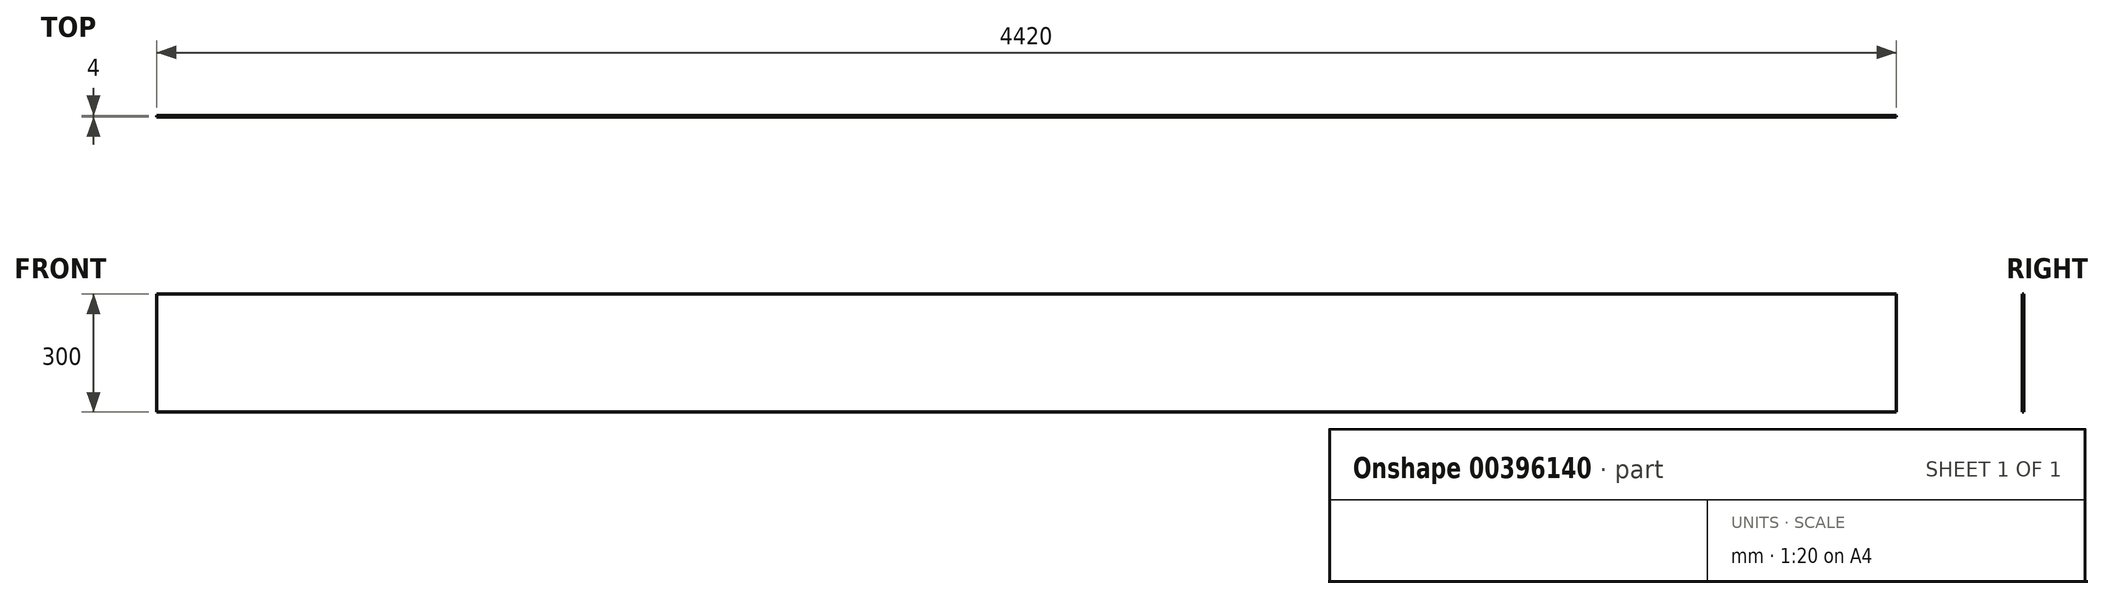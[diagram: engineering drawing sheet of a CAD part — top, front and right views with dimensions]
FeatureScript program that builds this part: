
annotation { "Feature Type Name" : "Feature", "Feature Type Description" : "" }
export const myFeature = defineFeature(function(context is Context, id is Id, definition is map)
    precondition{}
    {
        {
            var Q0;
            Q0=qCreatedBy(makeId("Front.planeOp"),FACE);
            var sketch = newSketch(context, id + "F0", { "sketchPlane" : qUnion([Q0])});
            skLineSegment(sketch, "E0.bottom", {"start": v(-2210, -150) * mm, "end": v(2210, -150) * mm});
            skLineSegment(sketch, "E0.top", {"start": v(-2210, 150) * mm, "end": v(2210, 150) * mm});
            skLineSegment(sketch, "E0.left", {"start": v(-2210, -150) * mm, "end": v(-2210, 150) * mm});
            skLineSegment(sketch, "E0.right", {"start": v(2210, -150) * mm, "end": v(2210, 150) * mm});
            skPoint(sketch, "E0.middle", {"position": v(0, 0) * mm});
            skLineSegment(sketch, "E1", {"start": v(3184.1, 0) * mm, "end": v(-3275.7, 0) * mm, "construction": true});
            skLineSegment(sketch, "E2", {"start": v(0, 380.68) * mm, "end": v(0, -287.6) * mm, "construction": true});
            skSolve(sketch);
        }
        {
            var Q0;
            Q0 = qSketchRegion(id + "F0", true);
            extrude(context, id + "F1", {"entities" : qUnion([Q0]), "depth" : 4 * mm});
        }
    });
